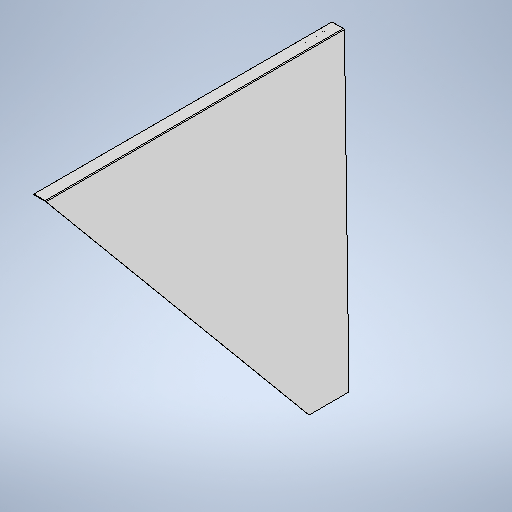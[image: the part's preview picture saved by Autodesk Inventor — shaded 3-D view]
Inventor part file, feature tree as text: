
AUTODESK INVENTOR PART (.ipt)
format: ipt  version: 2025 (Build 290162010, 162A)  size: 410,112 bytes
history: native  units: mm
features: other x7, sheet_metal_op x3, sketch x3, reference x2, extrude x1
ambient origin geometry x8: Origin, YZ Plane, XZ Plane, XY Plane, X Axis, Y Axis, Z Axis, Center Point
bodies: Solid1 (feature_tree)
feature tree (16):
  sheet_metal_op  "Contour Flange1"
  extrude  "Extrusion9"  Depth=4.0mm
  other  "Mark2"
  other  "A-Side Definition"
  sketch  "Sketch1"  dims[d6=4.0mm d7=4.0mm]
  other  "Plate1"
  sheet_metal_op  "Bend1"
  sheet_metal_op  "Corner1"
  sketch  "Sketch12"  dims[d8=2.0mm]
  reference  "Reference1"
  reference  "Reference2"
  sketch  "Sketch14"  dims[d9=8.0mm d10=6.0mm d11=1500.0mm d12=6.0mm d13=4.0mm d14=16.0mm d15=4.0mm d16=6.0mm d61=100.0mm d65=230.0mm d66=1150.0mm d68=60.0mm d70=6.0mm d79=775.0mm d81=6.0mm d82=0.0mm d83=0.0mm]
  other  "ASY MSC 100 cone.iam"
  other  "MSC 114 cone IN right board.ipt:1"
  other  "MSC 113 cone IN left board.ipt:1"
  other  "Definition1"
